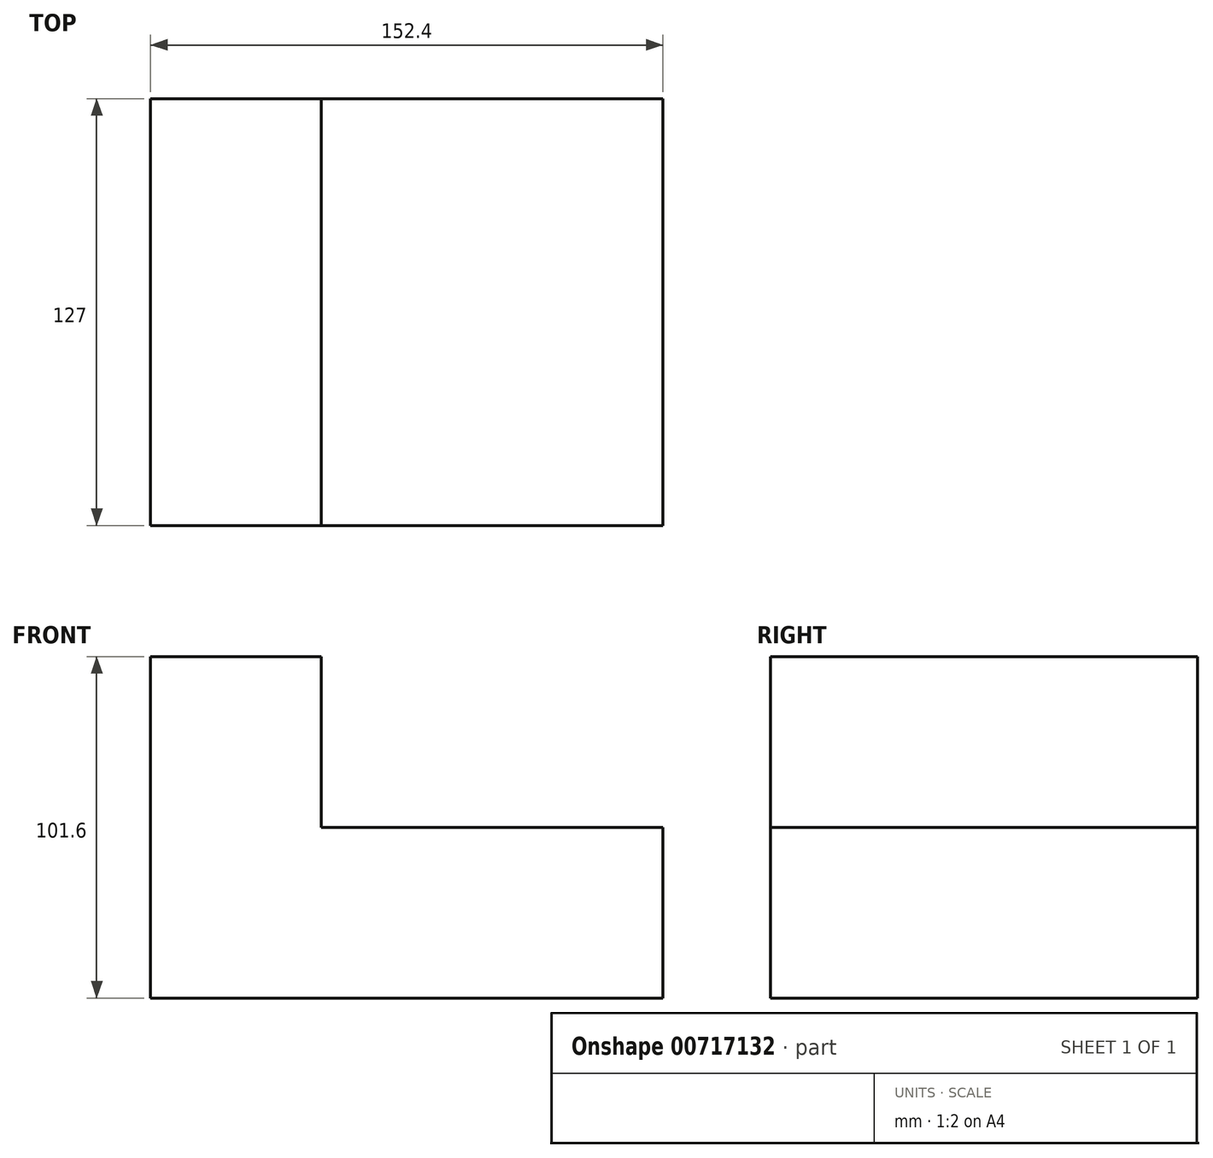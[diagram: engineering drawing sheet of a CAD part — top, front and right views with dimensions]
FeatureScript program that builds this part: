
annotation { "Feature Type Name" : "Feature", "Feature Type Description" : "" }
export const myFeature = defineFeature(function(context is Context, id is Id, definition is map)
    precondition{}
    {
        {
            var Q0;
            Q0=qCreatedBy(makeId("Front.planeOp"),FACE);
            var sketch = newSketch(context, id + "F0", { "sketchPlane" : qUnion([Q0])});
            skLineSegment(sketch, "E0", {"start": v(-131.47, -49.32) * mm, "end": v(20.93, -49.32) * mm});
            skLineSegment(sketch, "E1", {"start": v(20.93, -49.32) * mm, "end": v(20.93, 1.48) * mm});
            skLineSegment(sketch, "E2", {"start": v(20.93, 1.48) * mm, "end": v(-80.67, 1.48) * mm});
            skLineSegment(sketch, "E3", {"start": v(-80.67, 1.48) * mm, "end": v(-80.67, 52.28) * mm});
            skLineSegment(sketch, "E4", {"start": v(-80.67, 52.28) * mm, "end": v(-131.47, 52.28) * mm});
            skLineSegment(sketch, "E5", {"start": v(-131.47, 52.28) * mm, "end": v(-131.47, -49.32) * mm});
            skSolve(sketch);
        }
        {
            var Q0;
            Q0=makeQuery(id+"F0.imprint","IMPRINT",FACE,{"disambiguationData":[TD([[makeQuery(id+"F0.imprint","IMPRINT",EDGE,{"derivedFrom":sQuery(id+"F0.wireOp",EDGE,"E0")}),1.0]])]});
            extrude(context, id + "F1", {"entities" : qUnion([Q0]), "depth" : 127 * mm, "offsetDistance" : 25.4 * mm});
        }
    });
